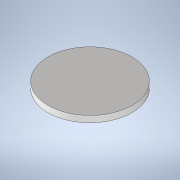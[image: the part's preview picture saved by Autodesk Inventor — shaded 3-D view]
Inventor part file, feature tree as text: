
AUTODESK INVENTOR PART (.ipt)
format: ipt  version: 2022 (Build 260153000, 153)  size: 113,152 bytes
history: native  units: mm
features: extrude x3, sketch x3
ambient origin geometry x8: Origin, YZ Plane, XZ Plane, XY Plane, X Axis, Y Axis, Z Axis, Center Point
bodies: Solid1 (feature_tree)
feature tree (6):
  extrude  "Extrusion1"  Depth=8.75mm
  extrude  "Extrusion2"  Depth=0.6mm TaperAngle=0.0deg
  extrude  "Extrusion3"  Depth=2.4mm TaperAngle=0.0deg
  sketch  "Sketch1"  dims[d0=6.0mm d1=8.75mm]
  sketch  "Sketch2"  dims[d2=2.7mm d3=0.0mm d4=0.6mm d5=0.0mm]
  sketch  "Sketch3"  dims[d6=31.6mm d7=2.4mm d8=0.0mm]
